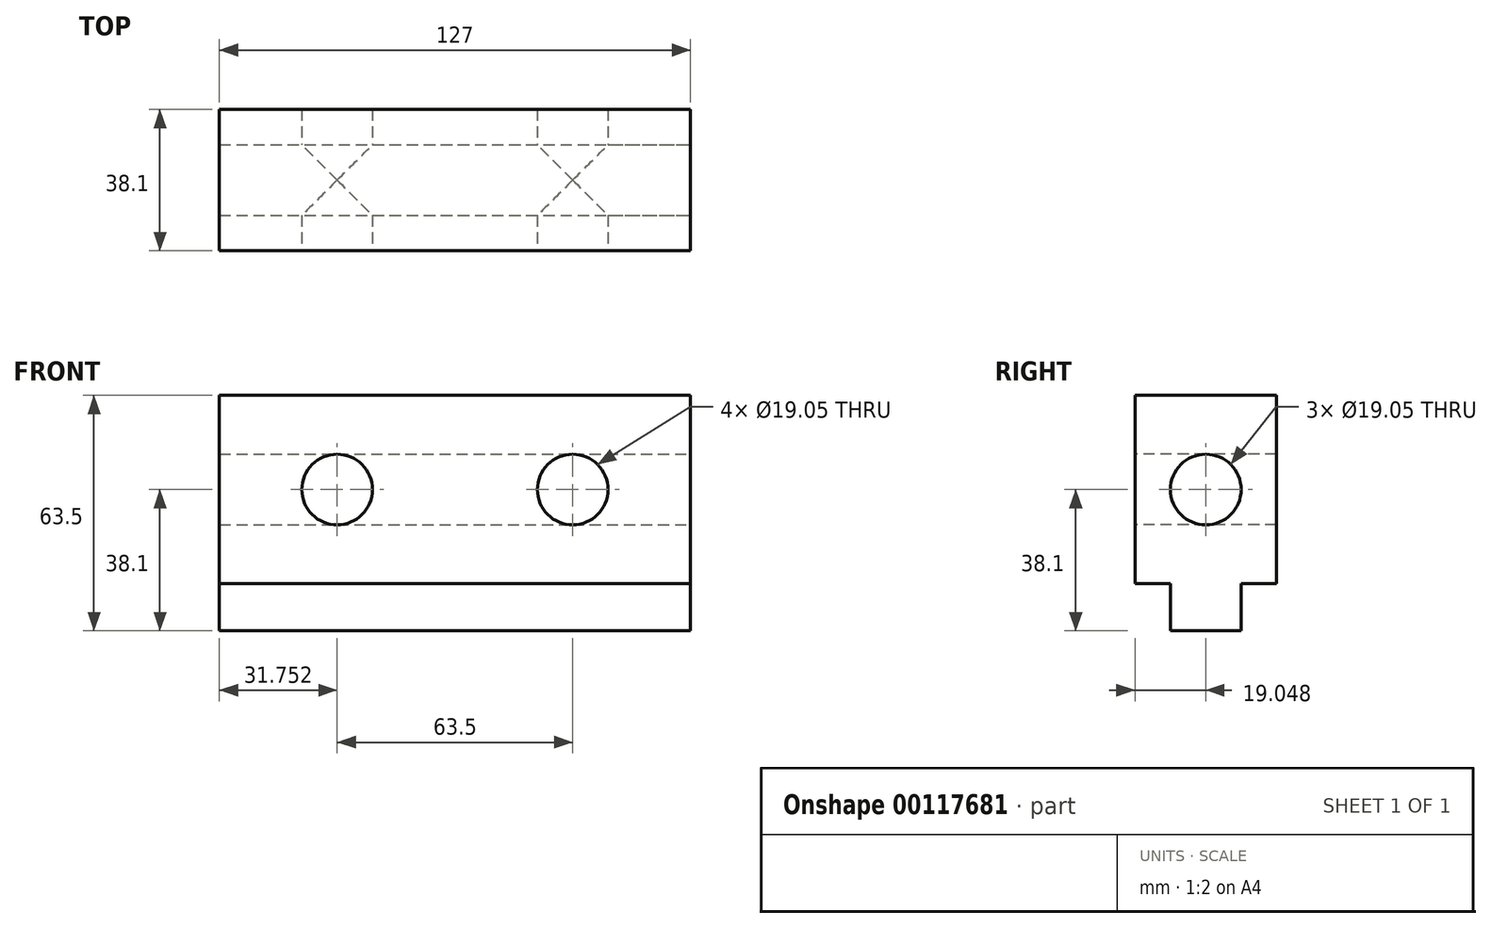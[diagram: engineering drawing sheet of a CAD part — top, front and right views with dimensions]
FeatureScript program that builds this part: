
annotation { "Feature Type Name" : "Feature", "Feature Type Description" : "" }
export const myFeature = defineFeature(function(context is Context, id is Id, definition is map)
    precondition{}
    {
        {
            var Q0;
            Q0=qCreatedBy(makeId("Top.planeOp"),FACE);
            var sketch = newSketch(context, id + "F0", { "sketchPlane" : qUnion([Q0])});
            skLineSegment(sketch, "E0.bottom", {"start": v(-83.64, 6.19) * mm, "end": v(43.36, 6.19) * mm});
            skLineSegment(sketch, "E0.top", {"start": v(-83.64, -31.91) * mm, "end": v(43.36, -31.91) * mm});
            skLineSegment(sketch, "E0.left", {"start": v(-83.64, 6.19) * mm, "end": v(-83.64, -31.91) * mm});
            skLineSegment(sketch, "E0.right", {"start": v(43.36, 6.19) * mm, "end": v(43.36, -31.91) * mm});
            skSolve(sketch);
        }
        {
            var Q0;
            Q0 = qSketchRegion(id + "F0", true);
            extrude(context, id + "F1", {"entities" : qUnion([Q0]), "depth" : 63.5 * mm});
        }
        {
            var Q0;
            Q0=makeQuery(id+"F1.opExtrude","SWEPT_FACE",FACE,{"disambiguationData":[OSD([sQuery(id+"F0.wireOp",EDGE,"E0.right")])]});
            var sketch = newSketch(context, id + "F2", { "sketchPlane" : qUnion([Q0])});
            skLineSegment(sketch, "E1.bottom", {"start": v(-31.91, 0) * mm, "end": v(-22.39, 0) * mm});
            skLineSegment(sketch, "E1.top", {"start": v(-31.91, 12.7) * mm, "end": v(-22.39, 12.7) * mm});
            skLineSegment(sketch, "E1.left", {"start": v(-31.91, 0) * mm, "end": v(-31.91, 12.7) * mm});
            skLineSegment(sketch, "E1.right", {"start": v(-22.39, 0) * mm, "end": v(-22.39, 12.7) * mm});
            skSolve(sketch);
        }
        {
            var Q0;
            Q0 = qSketchRegion(id + "F2", true);
            extrude(context, id + "F3", {"entities" : qUnion([Q0]), "operationType" : NewBodyOperationType.REMOVE, "endBound" : BoundingType.THROUGH_ALL, "oppositeDirection" : true, "depth" : 25.4 * mm});
        }
        {
            var Q0;
            Q0=makeQuery(id+"F1.opExtrude","SWEPT_FACE",FACE,{"disambiguationData":[OSD([sQuery(id+"F0.wireOp",EDGE,"E0.right")])]});
            var sketch = newSketch(context, id + "F4", { "sketchPlane" : qUnion([Q0])});
            skLineSegment(sketch, "E2.bottom", {"start": v(6.19, 0) * mm, "end": v(-3.34, 0) * mm});
            skLineSegment(sketch, "E2.top", {"start": v(6.19, 12.7) * mm, "end": v(-3.34, 12.7) * mm});
            skLineSegment(sketch, "E2.left", {"start": v(6.19, 0) * mm, "end": v(6.19, 12.7) * mm});
            skLineSegment(sketch, "E2.right", {"start": v(-3.34, 0) * mm, "end": v(-3.34, 12.7) * mm});
            skSolve(sketch);
        }
        {
            var Q0;
            Q0 = qSketchRegion(id + "F4", true);
            extrude(context, id + "F5", {"entities" : qUnion([Q0]), "operationType" : NewBodyOperationType.REMOVE, "endBound" : BoundingType.THROUGH_ALL, "oppositeDirection" : true, "depth" : 25.4 * mm});
        }
        {
            var Q0;
            Q0=makeQuery(id+"F1.opExtrude","SWEPT_FACE",FACE,{"disambiguationData":[OSD([sQuery(id+"F0.wireOp",EDGE,"E0.right")])]});
            var sketch = newSketch(context, id + "F6", { "sketchPlane" : qUnion([Q0])});
            skCircle(sketch, "E3", {"center": v(-12.86, 38.1) * mm, "radius": 9.53 * mm});
            skSolve(sketch);
        }
        {
            var Q0;
            Q0 = qSketchRegion(id + "F6", true);
            extrude(context, id + "F7", {"entities" : qUnion([Q0]), "operationType" : NewBodyOperationType.REMOVE, "endBound" : BoundingType.THROUGH_ALL, "oppositeDirection" : true, "depth" : 25.4 * mm});
        }
        {
            var Q0;
            Q0=makeQuery(id+"F1.opExtrude","SWEPT_FACE",FACE,{"disambiguationData":[OSD([sQuery(id+"F0.wireOp",EDGE,"E0.top")])]});
            var sketch = newSketch(context, id + "F8", { "sketchPlane" : qUnion([Q0])});
            skCircle(sketch, "E4", {"center": v(-51.89, 38.1) * mm, "radius": 9.53 * mm});
            skSolve(sketch);
        }
        {
            var Q0;
            Q0 = qSketchRegion(id + "F8", true);
            extrude(context, id + "F9", {"entities" : qUnion([Q0]), "operationType" : NewBodyOperationType.REMOVE, "endBound" : BoundingType.THROUGH_ALL, "oppositeDirection" : true, "depth" : 25.4 * mm});
        }
        {
            var Q0;
            Q0=makeQuery(id+"F1.opExtrude","SWEPT_FACE",FACE,{"disambiguationData":[OSD([sQuery(id+"F0.wireOp",EDGE,"E0.top")])]});
            var sketch = newSketch(context, id + "F10", { "sketchPlane" : qUnion([Q0])});
            skCircle(sketch, "E5", {"center": v(11.61, 38.1) * mm, "radius": 9.53 * mm});
            skSolve(sketch);
        }
        {
            var Q0;
            Q0 = qSketchRegion(id + "F10", true);
            extrude(context, id + "F11", {"entities" : qUnion([Q0]), "operationType" : NewBodyOperationType.REMOVE, "endBound" : BoundingType.THROUGH_ALL, "oppositeDirection" : true, "depth" : 25.4 * mm});
        }
    });
